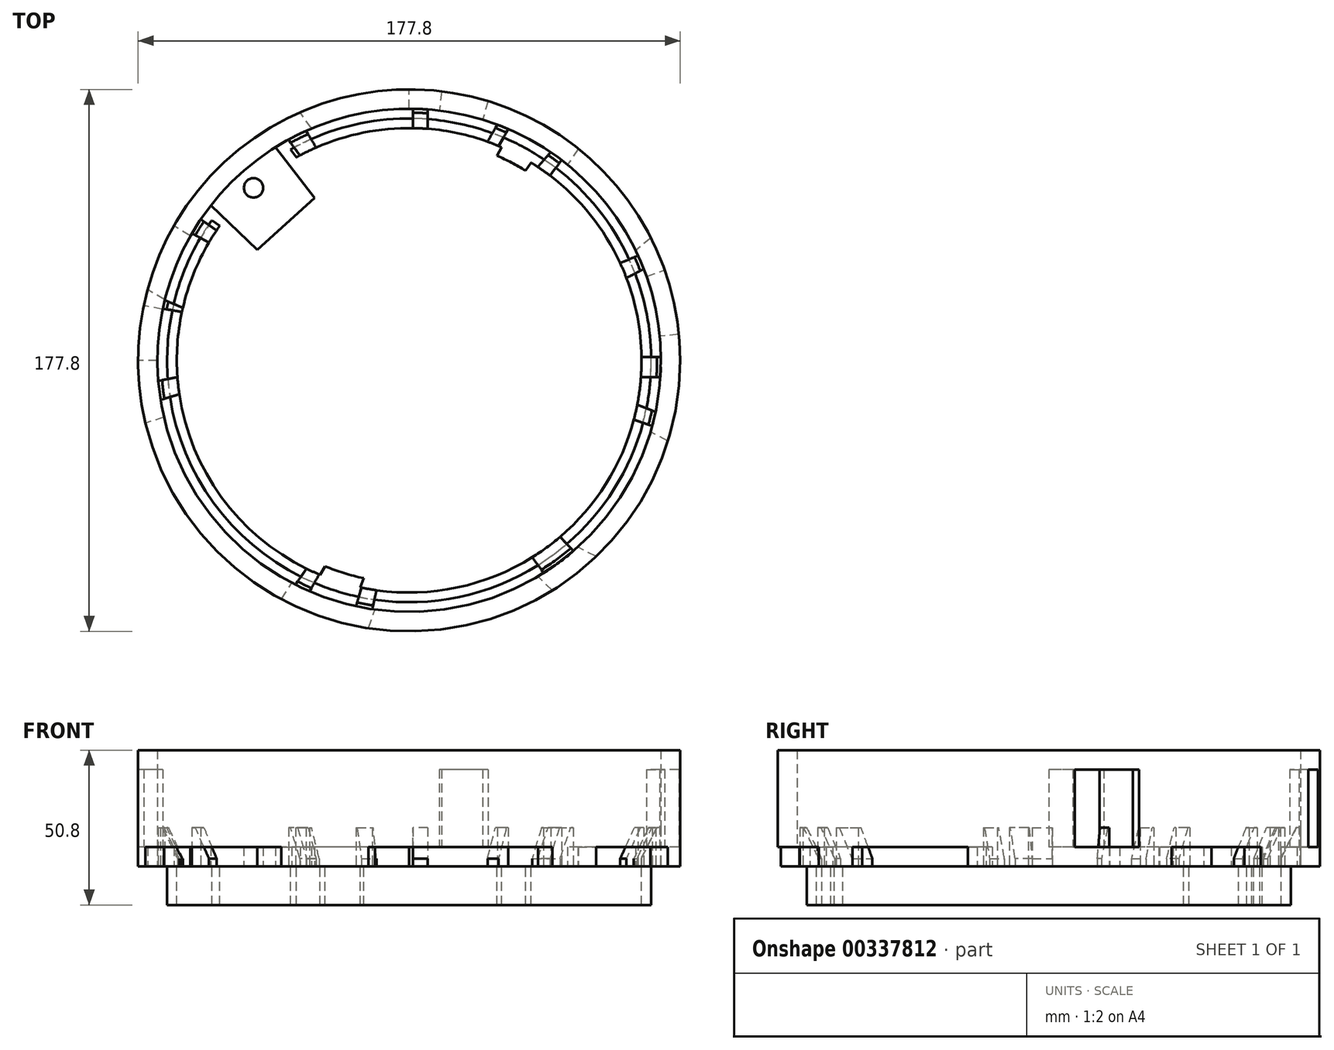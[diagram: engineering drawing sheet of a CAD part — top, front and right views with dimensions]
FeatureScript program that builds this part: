
annotation { "Feature Type Name" : "Feature", "Feature Type Description" : "" }
export const myFeature = defineFeature(function(context is Context, id is Id, definition is map)
    precondition{}
    {
        {
            var Q0;
            Q0=qCreatedBy(makeId("Top.planeOp"),FACE);
            var sketch = newSketch(context, id + "F0", { "sketchPlane" : qUnion([Q0])});
            skArc(sketch, "E0", {"start": v(-85.82, 23.2) * mm, "mid": v(-88.89, 1.33) * mm, "end": v(-86.48, -20.62) * mm});
            skArc(sketch, "E1", {"start": v(-65.06, 50.81) * mm, "mid": v(-68.6, 45.92) * mm, "end": v(-71.78, 40.77) * mm});
            skLineSegment(sketch, "E2", {"start": v(-40.4, 44.8) * mm, "end": v(-30.97, 53.31) * mm});
            skLineSegment(sketch, "E3", {"start": v(-40.4, 44.8) * mm, "end": v(-49.83, 36.3) * mm});
            skLineSegment(sketch, "E4", {"start": v(-49.83, 36.3) * mm, "end": v(-65.06, 50.81) * mm});
            skLineSegment(sketch, "E5", {"start": v(-30.97, 53.31) * mm, "end": v(-43.84, 69.95) * mm});
            skCircle(sketch, "E6", {"center": v(-51.04, 56.58) * mm, "radius": 3.18 * mm});
            skLineSegment(sketch, "E7", {"start": v(-41.98, -78.36) * mm, "end": v(-38.47, -73.04) * mm});
            skLineSegment(sketch, "E8", {"start": v(-13.4, -87.88) * mm, "end": v(-11.22, -81.78) * mm});
            skLineSegment(sketch, "E9", {"start": v(46.91, -75.52) * mm, "end": v(42.21, -70.94) * mm});
            skLineSegment(sketch, "E10", {"start": v(61.3, -64.38) * mm, "end": v(55.28, -61.3) * mm});
            skLineSegment(sketch, "E11", {"start": v(84.85, -26.52) * mm, "end": v(79.14, -23.49) * mm});
            skLineSegment(sketch, "E12", {"start": v(0, 82.55) * mm, "end": v(0, 88.9) * mm});
            skLineSegment(sketch, "E13", {"start": v(-32.04, 76.08) * mm, "end": v(-35.75, 81.4) * mm});
            skLineSegment(sketch, "E14", {"start": v(-71.78, 40.77) * mm, "end": v(-77.18, 44.11) * mm});
            skLineSegment(sketch, "E15", {"start": v(-80.12, 19.9) * mm, "end": v(-85.82, 23.2) * mm});
            skArc(sketch, "E16.trimOffspring", {"start": v(-80.12, 19.9) * mm, "mid": v(-82.55, 0.66) * mm, "end": v(-80.42, -18.62) * mm});
            skArc(sketch, "E17.trimOffspring", {"start": v(-32.04, 76.08) * mm, "mid": v(-38.06, 73.25) * mm, "end": v(-43.84, 69.95) * mm});
            skArc(sketch, "E18.trimOffspring", {"start": v(-35.75, 81.4) * mm, "mid": v(-59.47, 66.08) * mm, "end": v(-77.18, 44.11) * mm});
            skArc(sketch, "E19.trimOffspring", {"start": v(79.14, -23.49) * mm, "mid": v(82.28, 6.71) * mm, "end": v(74.28, 36) * mm});
            skArc(sketch, "E20.trimOffspring", {"start": v(84.85, -26.52) * mm, "mid": v(88.6, 7.4) * mm, "end": v(79.28, 40.22) * mm});
            skArc(sketch, "E21.trimOffspring", {"start": v(42.21, -70.94) * mm, "mid": v(48.98, -66.45) * mm, "end": v(55.28, -61.3) * mm});
            skArc(sketch, "E22.trimOffspring", {"start": v(46.91, -75.52) * mm, "mid": v(54.4, -70.32) * mm, "end": v(61.3, -64.38) * mm});
            skArc(sketch, "E23.trimOffspring", {"start": v(-41.98, -78.36) * mm, "mid": v(-28.1, -84.34) * mm, "end": v(-13.4, -87.88) * mm});
            skArc(sketch, "E24.trimOffspring", {"start": v(-38.47, -73.04) * mm, "mid": v(-25.23, -78.6) * mm, "end": v(-11.22, -81.78) * mm});
            skLineSegment(sketch, "E25", {"start": v(55.5, 69.45) * mm, "end": v(51.94, 64.16) * mm});
            skLineSegment(sketch, "E26", {"start": v(79.28, 40.22) * mm, "end": v(74.28, 36) * mm});
            skArc(sketch, "E27.trimOffspring", {"start": v(55.5, 69.45) * mm, "mid": v(29.4, 83.9) * mm, "end": v(0, 88.9) * mm});
            skArc(sketch, "E28.trimOffspring", {"start": v(51.94, 64.16) * mm, "mid": v(27.55, 77.82) * mm, "end": v(0, 82.55) * mm});
            skLineSegment(sketch, "E29", {"start": v(-80.42, -18.62) * mm, "end": v(-86.48, -20.62) * mm});
            skSolve(sketch);
        }
        {
            var Q0;
            Q0=makeQuery(id+"F0.imprint","IMPRINT",FACE,{"disambiguationData":[TD([[makeQuery(id+"F0.imprint","IMPRINT",EDGE,{"derivedFrom":sQuery(id+"F0.wireOp",EDGE,"E0")}),1.0]])]});
            extrude(context, id + "F1", {"entities" : qUnion([Q0]), "depth" : 6.35 * mm});
        }
        {
            var Q0;
            Q0=qCreatedBy(makeId("Top.planeOp"),FACE);
            var sketch = newSketch(context, id + "F2", { "sketchPlane" : qUnion([Q0])});
            skArc(sketch, "E30", {"start": v(-88.9, 0) * mm, "mid": v(4.26, -88.8) * mm, "end": v(88.5, 8.52) * mm});
            skArc(sketch, "E31", {"start": v(-82.55, 0) * mm, "mid": v(3.96, -82.46) * mm, "end": v(82.17, 7.9) * mm});
            skLineSegment(sketch, "E32", {"start": v(-82.55, 0) * mm, "end": v(-88.9, 0) * mm});
            skLineSegment(sketch, "E33", {"start": v(-80.85, 16.68) * mm, "end": v(-87.07, 17.96) * mm});
            skLineSegment(sketch, "E34", {"start": v(25.92, 85.04) * mm, "end": v(24.07, 78.96) * mm});
            skLineSegment(sketch, "E35", {"start": v(10.66, 88.26) * mm, "end": v(9.9, 81.95) * mm});
            skLineSegment(sketch, "E36", {"start": v(77.84, 27.5) * mm, "end": v(83.82, 29.61) * mm});
            skLineSegment(sketch, "E37", {"start": v(88.5, 8.52) * mm, "end": v(82.17, 7.9) * mm});
            skArc(sketch, "E38.trimOffspring", {"start": v(10.66, 88.26) * mm, "mid": v(-51.91, 72.17) * mm, "end": v(-87.07, 17.96) * mm});
            skArc(sketch, "E39.trimOffspring", {"start": v(9.9, 81.95) * mm, "mid": v(-48.2, 67.01) * mm, "end": v(-80.85, 16.68) * mm});
            skArc(sketch, "E40.trimOffspring", {"start": v(77.84, 27.5) * mm, "mid": v(57.08, 59.63) * mm, "end": v(24.07, 78.96) * mm});
            skArc(sketch, "E41.trimOffspring", {"start": v(83.82, 29.61) * mm, "mid": v(61.47, 64.22) * mm, "end": v(25.92, 85.04) * mm});
            skSolve(sketch);
        }
        {
            var Q0;
            Q0 = qSketchRegion(id + "F2", true);
            extrude(context, id + "F3", {"entities" : qUnion([Q0]), "operationType" : NewBodyOperationType.ADD, "depth" : 31.75 * mm, "hasSecondDirection" : true, "secondDirectionOppositeDirection" : true, "secondDirectionDepth" : -6.35 * mm});
        }
        {
            var Q0;
            Q0=qCreatedBy(makeId("Top.planeOp"),FACE);
            var sketch = newSketch(context, id + "F4", { "sketchPlane" : qUnion([Q0])});
            skCircle(sketch, "E42", {"center": v(0, 0) * mm, "radius": 88.9 * mm});
            skCircle(sketch, "E43", {"center": v(0, 0) * mm, "radius": 82.55 * mm});
            skSolve(sketch);
        }
        {
            var Q0;
            Q0 = qSketchRegion(id + "F4", true);
            extrude(context, id + "F5", {"entities" : qUnion([Q0]), "operationType" : NewBodyOperationType.ADD, "depth" : 38.1 * mm, "hasSecondDirection" : true, "secondDirectionOppositeDirection" : true, "secondDirectionDepth" : -31.75 * mm});
        }
        {
            var Q0;
            Q0=qCreatedBy(makeId("Top.planeOp"),FACE);
            var sketch = newSketch(context, id + "F6", { "sketchPlane" : qUnion([Q0])});
            skCircle(sketch, "E44", {"center": v(0, 0) * mm, "radius": 82.55 * mm});
            skArc(sketch, "E45", {"start": v(-64.74, 45.93) * mm, "mid": v(53.13, -58.97) * mm, "end": v(-38.95, 69.16) * mm});
            skArc(sketch, "E46", {"start": v(-62.13, 44.11) * mm, "mid": v(50.85, -56.75) * mm, "end": v(-37.05, 66.59) * mm});
            skLineSegment(sketch, "E47", {"start": v(-64.74, 45.93) * mm, "end": v(-62.13, 44.11) * mm});
            skLineSegment(sketch, "E48", {"start": v(-38.95, 69.16) * mm, "end": v(-37.05, 66.59) * mm});
            skSolve(sketch);
        }
        {
            var Q0;
            Q0=makeQuery(id+"F6.imprint","IMPRINT",FACE,{"disambiguationData":[TD([[makeQuery(id+"F6.imprint","IMPRINT",EDGE,{"derivedFrom":sQuery(id+"F6.wireOp",EDGE,"E45")}),1.0]])]});
            extrude(context, id + "F7", {"entities" : qUnion([Q0]), "operationType" : NewBodyOperationType.ADD, "oppositeDirection" : true, "depth" : 12.7 * mm});
        }
        {
            var Q0;
            Q0 = qSketchRegion(id + "F0", true);
            extrude(context, id + "F8", {"entities" : qUnion([Q0]), "operationType" : NewBodyOperationType.ADD, "depth" : 6.35 * mm});
        }
        {
            var Q0;
            Q0=qCreatedBy(makeId("Top.planeOp"),FACE);
            var sketch = newSketch(context, id + "F9", { "sketchPlane" : qUnion([Q0])});
            skArc(sketch, "E49", {"start": v(-80.15, 19.76) * mm, "mid": v(-80.48, 18.36) * mm, "end": v(-80.79, 16.96) * mm});
            skArc(sketch, "E50", {"start": v(-74.22, 17.25) * mm, "mid": v(-74.38, 16.56) * mm, "end": v(-74.53, 15.87) * mm});
            skLineSegment(sketch, "E51", {"start": v(-80.15, 19.76) * mm, "end": v(-74.22, 17.25) * mm});
            skPoint(sketch, "E52.startSnap0", {"position": v(-77.19, 18.5) * mm});
            skLineSegment(sketch, "E53", {"start": v(-68.38, 46.24) * mm, "end": v(-63.16, 42.63) * mm});
            skLineSegment(sketch, "E54", {"start": v(-71.26, 41.68) * mm, "end": v(-65.68, 38.63) * mm});
            skLineSegment(sketch, "E55", {"start": v(-39.57, 72.45) * mm, "end": v(-35.9, 67.21) * mm});
            skLineSegment(sketch, "E56", {"start": v(-33.84, 75.3) * mm, "end": v(-30.5, 69.83) * mm});
            skLineSegment(sketch, "E57", {"start": v(-80.79, 16.96) * mm, "end": v(-74.53, 15.87) * mm});
            skLineSegment(sketch, "E58", {"start": v(-82.27, -6.77) * mm, "end": v(-76, -5.51) * mm});
            skLineSegment(sketch, "E59", {"start": v(-81.53, -12.97) * mm, "end": v(-75.38, -11.12) * mm});
            skLineSegment(sketch, "E60", {"start": v(-37.28, -73.65) * mm, "end": v(-33.65, -68.37) * mm});
            skLineSegment(sketch, "E61", {"start": v(-32.7, -75.8) * mm, "end": v(-29.5, -70.26) * mm});
            skLineSegment(sketch, "E62", {"start": v(-12.09, -81.66) * mm, "end": v(-10.72, -75.44) * mm});
            skLineSegment(sketch, "E63", {"start": v(-17.4, -80.7) * mm, "end": v(-15.67, -74.57) * mm});
            skLineSegment(sketch, "E64", {"start": v(44.09, -69.8) * mm, "end": v(40.4, -64.6) * mm});
            skLineSegment(sketch, "E65", {"start": v(53.87, -62.55) * mm, "end": v(49.52, -57.92) * mm});
            skLineSegment(sketch, "E66", {"start": v(82.54, 1.07) * mm, "end": v(76.2, 1.07) * mm});
            skLineSegment(sketch, "E67", {"start": v(82.37, -5.52) * mm, "end": v(76, -5.52) * mm});
            skLineSegment(sketch, "E68", {"start": v(79.7, -21.54) * mm, "end": v(73.67, -19.46) * mm});
            skLineSegment(sketch, "E69", {"start": v(80.8, -16.9) * mm, "end": v(74.8, -14.58) * mm});
            skLineSegment(sketch, "E70", {"start": v(76.92, 29.96) * mm, "end": v(71.25, 27) * mm});
            skLineSegment(sketch, "E71", {"start": v(75.05, 34.39) * mm, "end": v(69.2, 31.88) * mm});
            skLineSegment(sketch, "E72", {"start": v(50.02, 65.67) * mm, "end": v(46.16, 60.63) * mm});
            skLineSegment(sketch, "E73", {"start": v(46.39, 68.28) * mm, "end": v(42.18, 63.46) * mm});
            skLineSegment(sketch, "E74", {"start": v(6.09, 82.33) * mm, "end": v(6.09, 75.96) * mm});
            skLineSegment(sketch, "E75", {"start": v(1.2, 82.54) * mm, "end": v(1.2, 76.2) * mm});
            skLineSegment(sketch, "E76", {"start": v(28.9, 77.33) * mm, "end": v(25.7, 71.74) * mm});
            skLineSegment(sketch, "E77", {"start": v(32.52, 75.87) * mm, "end": v(29.33, 70.33) * mm});
            skArc(sketch, "E78.trimOffspring", {"start": v(-68.38, 46.24) * mm, "mid": v(-69.86, 43.98) * mm, "end": v(-71.26, 41.68) * mm});
            skArc(sketch, "E79.trimOffspring", {"start": v(-63.16, 42.63) * mm, "mid": v(-64.45, 40.65) * mm, "end": v(-65.68, 38.63) * mm});
            skArc(sketch, "E80.trimOffspring", {"start": v(-82.27, -6.77) * mm, "mid": v(-81.96, -9.87) * mm, "end": v(-81.53, -12.97) * mm});
            skArc(sketch, "E81.trimOffspring", {"start": v(-76, -5.51) * mm, "mid": v(-75.74, -8.32) * mm, "end": v(-75.38, -11.12) * mm});
            skArc(sketch, "E82.trimOffspring", {"start": v(-37.28, -73.65) * mm, "mid": v(-35.01, -74.76) * mm, "end": v(-32.7, -75.8) * mm});
            skArc(sketch, "E83.trimOffspring", {"start": v(-33.65, -68.37) * mm, "mid": v(-31.6, -69.34) * mm, "end": v(-29.5, -70.26) * mm});
            skArc(sketch, "E84.trimOffspring", {"start": v(-17.4, -80.7) * mm, "mid": v(-14.76, -81.22) * mm, "end": v(-12.09, -81.66) * mm});
            skArc(sketch, "E85.trimOffspring", {"start": v(-15.67, -74.57) * mm, "mid": v(-13.2, -75.05) * mm, "end": v(-10.72, -75.44) * mm});
            skArc(sketch, "E86.trimOffspring", {"start": v(40.4, -64.6) * mm, "mid": v(45.08, -61.43) * mm, "end": v(49.52, -57.92) * mm});
            skArc(sketch, "E87.trimOffspring", {"start": v(44.09, -69.8) * mm, "mid": v(49.11, -66.35) * mm, "end": v(53.87, -62.55) * mm});
            skArc(sketch, "E88.trimOffspring", {"start": v(73.67, -19.46) * mm, "mid": v(74.27, -17.03) * mm, "end": v(74.8, -14.58) * mm});
            skArc(sketch, "E89.trimOffspring", {"start": v(79.7, -21.54) * mm, "mid": v(80.28, -19.22) * mm, "end": v(80.8, -16.9) * mm});
            skArc(sketch, "E90.trimOffspring", {"start": v(76, -5.52) * mm, "mid": v(76.17, -2.23) * mm, "end": v(76.2, 1.07) * mm});
            skArc(sketch, "E91.trimOffspring", {"start": v(82.37, -5.52) * mm, "mid": v(82.52, -2.23) * mm, "end": v(82.54, 1.07) * mm});
            skArc(sketch, "E92.trimOffspring", {"start": v(71.25, 27) * mm, "mid": v(70.27, 29.46) * mm, "end": v(69.2, 31.88) * mm});
            skArc(sketch, "E93.trimOffspring", {"start": v(76.92, 29.96) * mm, "mid": v(76.02, 32.19) * mm, "end": v(75.05, 34.39) * mm});
            skArc(sketch, "E94.trimOffspring", {"start": v(46.16, 60.63) * mm, "mid": v(44.2, 62.08) * mm, "end": v(42.18, 63.46) * mm});
            skArc(sketch, "E95.trimOffspring", {"start": v(50.02, 65.67) * mm, "mid": v(48.22, 67) * mm, "end": v(46.39, 68.28) * mm});
            skArc(sketch, "E96.trimOffspring", {"start": v(29.33, 70.33) * mm, "mid": v(27.52, 71.06) * mm, "end": v(25.7, 71.74) * mm});
            skArc(sketch, "E97.trimOffspring", {"start": v(32.52, 75.87) * mm, "mid": v(30.72, 76.62) * mm, "end": v(28.9, 77.33) * mm});
            skArc(sketch, "E98.trimOffspring", {"start": v(6.09, 82.33) * mm, "mid": v(3.65, 82.47) * mm, "end": v(1.2, 82.54) * mm});
            skArc(sketch, "E99.trimOffspring", {"start": v(6.09, 75.96) * mm, "mid": v(3.65, 76.11) * mm, "end": v(1.2, 76.2) * mm});
            skArc(sketch, "E100.trimOffspring", {"start": v(-30.5, 69.83) * mm, "mid": v(-33.23, 68.57) * mm, "end": v(-35.9, 67.21) * mm});
            skArc(sketch, "E101.trimOffspring", {"start": v(-33.84, 75.3) * mm, "mid": v(-36.74, 73.93) * mm, "end": v(-39.57, 72.45) * mm});
            skSolve(sketch);
        }
        {
            var Q0;
            Q0=makeQuery(id+"F9.imprint","IMPRINT",FACE,{"disambiguationData":[TD([[makeQuery(id+"F9.imprint","IMPRINT",EDGE,{"derivedFrom":sQuery(id+"F9.wireOp",EDGE,"E55")}),1.0]])]});
            var Q1;
            Q1=makeQuery(id+"F9.imprint","IMPRINT",FACE,{"disambiguationData":[TD([[makeQuery(id+"F9.imprint","IMPRINT",EDGE,{"derivedFrom":sQuery(id+"F9.wireOp",EDGE,"E74")}),-1.0]])]});
            var Q2;
            Q2=makeQuery(id+"F9.imprint","IMPRINT",FACE,{"disambiguationData":[TD([[makeQuery(id+"F9.imprint","IMPRINT",EDGE,{"derivedFrom":sQuery(id+"F9.wireOp",EDGE,"E76")}),1.0]])]});
            var Q3;
            Q3=makeQuery(id+"F9.imprint","IMPRINT",FACE,{"disambiguationData":[TD([[makeQuery(id+"F9.imprint","IMPRINT",EDGE,{"derivedFrom":sQuery(id+"F9.wireOp",EDGE,"E72")}),-1.0]])]});
            var Q4;
            Q4=makeQuery(id+"F9.imprint","IMPRINT",FACE,{"disambiguationData":[TD([[makeQuery(id+"F9.imprint","IMPRINT",EDGE,{"derivedFrom":sQuery(id+"F9.wireOp",EDGE,"E70")}),-1.0]])]});
            var Q5;
            Q5=makeQuery(id+"F9.imprint","IMPRINT",FACE,{"disambiguationData":[TD([[makeQuery(id+"F9.imprint","IMPRINT",EDGE,{"derivedFrom":sQuery(id+"F9.wireOp",EDGE,"E66")}),1.0]])]});
            var Q6;
            Q6=makeQuery(id+"F9.imprint","IMPRINT",FACE,{"disambiguationData":[TD([[makeQuery(id+"F9.imprint","IMPRINT",EDGE,{"derivedFrom":sQuery(id+"F9.wireOp",EDGE,"E68")}),-1.0]])]});
            var Q7;
            Q7=makeQuery(id+"F9.imprint","IMPRINT",FACE,{"disambiguationData":[TD([[makeQuery(id+"F9.imprint","IMPRINT",EDGE,{"derivedFrom":sQuery(id+"F9.wireOp",EDGE,"E64")}),-1.0]])]});
            var Q8;
            Q8=makeQuery(id+"F9.imprint","IMPRINT",FACE,{"disambiguationData":[TD([[makeQuery(id+"F9.imprint","IMPRINT",EDGE,{"derivedFrom":sQuery(id+"F9.wireOp",EDGE,"E62")}),1.0]])]});
            var Q9;
            Q9=makeQuery(id+"F9.imprint","IMPRINT",FACE,{"disambiguationData":[TD([[makeQuery(id+"F9.imprint","IMPRINT",EDGE,{"derivedFrom":sQuery(id+"F9.wireOp",EDGE,"E60")}),-1.0]])]});
            var Q10;
            Q10=makeQuery(id+"F9.imprint","IMPRINT",FACE,{"disambiguationData":[TD([[makeQuery(id+"F9.imprint","IMPRINT",EDGE,{"derivedFrom":sQuery(id+"F9.wireOp",EDGE,"E58")}),-1.0]])]});
            var Q11;
            Q11=makeQuery(id+"F9.imprint","IMPRINT",FACE,{"disambiguationData":[TD([[makeQuery(id+"F9.imprint","IMPRINT",EDGE,{"derivedFrom":sQuery(id+"F9.wireOp",EDGE,"E49")}),1.0]])]});
            var Q12;
            Q12=makeQuery(id+"F9.imprint","IMPRINT",FACE,{"disambiguationData":[TD([[makeQuery(id+"F9.imprint","IMPRINT",EDGE,{"derivedFrom":sQuery(id+"F9.wireOp",EDGE,"E53")}),-1.0]])]});
            extrude(context, id + "F10", {"entities" : qUnion([Q0, Q1, Q2, Q3, Q4, Q5, Q6, Q7, Q8, Q9, Q10, Q11, Q12]), "operationType" : NewBodyOperationType.ADD, "depth" : 12.7 * mm});
        }
        {
            var Q0;
            Q0=makeQuery(id+"F10.opExtrude","CAP_EDGE",EDGE,{"disambiguationData":[OSD([sQuery(id+"F9.wireOp",EDGE,"E99.trimOffspring")])],"isStart":false});
            chamfer(context, id + "F11", {"entities" : qUnion([Q0]), "chamferType" : ChamferType.TWO_OFFSETS, "width1" : 10.16 * mm, "oppositeDirection" : false, "width2" : 5.08 * mm});
        }
        {
            var Q0;
            Q0=makeQuery(id+"F10.opExtrude","CAP_EDGE",EDGE,{"disambiguationData":[OSD([sQuery(id+"F9.wireOp",EDGE,"E96.trimOffspring")])],"isStart":false});
            chamfer(context, id + "F12", {"entities" : qUnion([Q0]), "chamferType" : ChamferType.TWO_OFFSETS, "width1" : 10.16 * mm, "oppositeDirection" : false, "width2" : 5.08 * mm, "tangentPropagation" : true});
        }
        {
            var Q0;
            Q0=makeQuery(id+"F10.opExtrude","CAP_EDGE",EDGE,{"disambiguationData":[OSD([sQuery(id+"F9.wireOp",EDGE,"E94.trimOffspring")])],"isStart":false});
            chamfer(context, id + "F13", {"entities" : qUnion([Q0]), "chamferType" : ChamferType.TWO_OFFSETS, "width1" : 10.16 * mm, "oppositeDirection" : false, "width2" : 5.08 * mm, "tangentPropagation" : true});
        }
        {
            var Q0;
            Q0=makeQuery(id+"F10.opExtrude","CAP_EDGE",EDGE,{"disambiguationData":[OSD([sQuery(id+"F9.wireOp",EDGE,"E92.trimOffspring")])],"isStart":false});
            chamfer(context, id + "F14", {"entities" : qUnion([Q0]), "chamferType" : ChamferType.TWO_OFFSETS, "width1" : 10.16 * mm, "oppositeDirection" : false, "width2" : 5.08 * mm, "tangentPropagation" : true});
        }
        {
            var Q0;
            Q0=makeQuery(id+"F10.opExtrude","CAP_EDGE",EDGE,{"disambiguationData":[OSD([sQuery(id+"F9.wireOp",EDGE,"E90.trimOffspring")])],"isStart":false});
            chamfer(context, id + "F15", {"entities" : qUnion([Q0]), "chamferType" : ChamferType.TWO_OFFSETS, "width1" : 10.16 * mm, "oppositeDirection" : false, "width2" : 5.08 * mm, "tangentPropagation" : true});
        }
        {
            var Q0;
            Q0=makeQuery(id+"F10.opExtrude","CAP_EDGE",EDGE,{"disambiguationData":[OSD([sQuery(id+"F9.wireOp",EDGE,"E88.trimOffspring")])],"isStart":false});
            chamfer(context, id + "F16", {"entities" : qUnion([Q0]), "chamferType" : ChamferType.TWO_OFFSETS, "width1" : 10.16 * mm, "oppositeDirection" : false, "width2" : 5.08 * mm, "tangentPropagation" : true});
        }
        {
            var Q0;
            Q0=makeQuery(id+"F10.opExtrude","CAP_EDGE",EDGE,{"disambiguationData":[OSD([sQuery(id+"F9.wireOp",EDGE,"E86.trimOffspring")])],"isStart":false});
            chamfer(context, id + "F17", {"entities" : qUnion([Q0]), "chamferType" : ChamferType.TWO_OFFSETS, "width1" : 10.16 * mm, "oppositeDirection" : false, "width2" : 5.08 * mm, "tangentPropagation" : true});
        }
        {
            var Q0;
            Q0=makeQuery(id+"F10.opExtrude","CAP_EDGE",EDGE,{"disambiguationData":[OSD([sQuery(id+"F9.wireOp",EDGE,"E85.trimOffspring")])],"isStart":false});
            chamfer(context, id + "F18", {"entities" : qUnion([Q0]), "chamferType" : ChamferType.TWO_OFFSETS, "width1" : 10.16 * mm, "oppositeDirection" : false, "width2" : 5.08 * mm, "tangentPropagation" : true});
        }
        {
            var Q0;
            Q0=makeQuery(id+"F10.opExtrude","CAP_EDGE",EDGE,{"disambiguationData":[OSD([sQuery(id+"F9.wireOp",EDGE,"E83.trimOffspring")])],"isStart":false});
            chamfer(context, id + "F19", {"entities" : qUnion([Q0]), "chamferType" : ChamferType.TWO_OFFSETS, "width1" : 10.16 * mm, "oppositeDirection" : false, "width2" : 5.08 * mm, "tangentPropagation" : true});
        }
        {
            var Q0;
            Q0=makeQuery(id+"F10.opExtrude","CAP_EDGE",EDGE,{"disambiguationData":[OSD([sQuery(id+"F9.wireOp",EDGE,"E81.trimOffspring")])],"isStart":false});
            var Q1;
            Q1=makeQuery(id+"F10.opExtrude","CAP_EDGE",EDGE,{"disambiguationData":[OSD([sQuery(id+"F9.wireOp",EDGE,"E50")])],"isStart":false});
            var Q2;
            Q2=makeQuery(id+"F10.opExtrude","CAP_EDGE",EDGE,{"disambiguationData":[OSD([sQuery(id+"F9.wireOp",EDGE,"E79.trimOffspring")])],"isStart":false});
            var Q3;
            Q3=makeQuery(id+"F10.opExtrude","CAP_EDGE",EDGE,{"disambiguationData":[OSD([sQuery(id+"F9.wireOp",EDGE,"E100.trimOffspring")])],"isStart":false});
            chamfer(context, id + "F20", {"entities" : qUnion([Q0, Q1, Q2, Q3]), "chamferType" : ChamferType.TWO_OFFSETS, "width1" : 10.16 * mm, "oppositeDirection" : false, "width2" : 5.08 * mm, "tangentPropagation" : true});
        }
        {
            var Q0;
            Q0=qCreatedBy(makeId("Top.planeOp"),FACE);
            var sketch = newSketch(context, id + "F21", { "sketchPlane" : qUnion([Q0])});
            skArc(sketch, "E102", {"start": v(-29.2, -70.38) * mm, "mid": v(-22.7, -72.74) * mm, "end": v(-16.02, -74.5) * mm});
            skArc(sketch, "E103", {"start": v(-27.65, -67.59) * mm, "mid": v(-21.4, -69.82) * mm, "end": v(-14.96, -71.48) * mm});
            skLineSegment(sketch, "E104", {"start": v(30.37, 69.89) * mm, "end": v(28.8, 67.1) * mm});
            skLineSegment(sketch, "E105", {"start": v(39.95, 64.89) * mm, "end": v(38.15, 62.27) * mm});
            skLineSegment(sketch, "E106", {"start": v(-29.2, -70.38) * mm, "end": v(-27.65, -67.59) * mm});
            skLineSegment(sketch, "E107", {"start": v(-16.02, -74.5) * mm, "end": v(-14.96, -71.48) * mm});
            skArc(sketch, "E108.trimOffspring", {"start": v(38.15, 62.27) * mm, "mid": v(33.56, 64.85) * mm, "end": v(28.8, 67.1) * mm});
            skArc(sketch, "E109.trimOffspring", {"start": v(39.95, 64.89) * mm, "mid": v(35.25, 67.56) * mm, "end": v(30.37, 69.89) * mm});
            skSolve(sketch);
        }
        {
            var Q0;
            Q0=makeQuery(id+"F21.imprint","IMPRINT",FACE,{"disambiguationData":[TD([[makeQuery(id+"F21.imprint","IMPRINT",EDGE,{"derivedFrom":sQuery(id+"F21.wireOp",EDGE,"E104")}),1.0]])]});
            var Q1;
            Q1=makeQuery(id+"F21.imprint","IMPRINT",FACE,{"disambiguationData":[TD([[makeQuery(id+"F21.imprint","IMPRINT",EDGE,{"derivedFrom":sQuery(id+"F21.wireOp",EDGE,"E102")}),1.0]])]});
            extrude(context, id + "F22", {"entities" : qUnion([Q0, Q1]), "operationType" : NewBodyOperationType.ADD, "oppositeDirection" : true, "depth" : 12.7 * mm});
        }
    });
